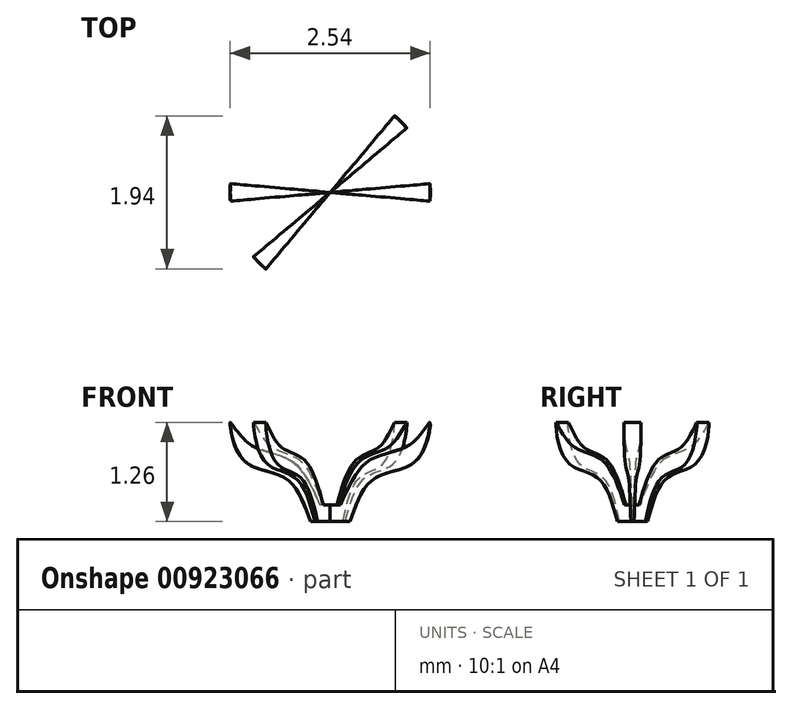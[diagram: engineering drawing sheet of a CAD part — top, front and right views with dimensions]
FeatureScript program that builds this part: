
annotation { "Feature Type Name" : "Feature", "Feature Type Description" : "" }
export const myFeature = defineFeature(function(context is Context, id is Id, definition is map)
    precondition{}
    {
        {
            var Q0;
            Q0=qCreatedBy(makeId("Front.planeOp"),FACE);
            var sketch = newSketch(context, id + "F0", { "sketchPlane" : qUnion([Q0])});
            skFitSpline(sketch, "E0", {"points": [v(-0.25, 0) * mm, v(-0.58, 0.55) * mm, v(-1.12, 0.8) * mm, v(-1.27, 1.25) * mm, v(-1.27, 1.26) * mm], "startDerivative": vector(-0.7, 1.99) * mm, "endDerivative": vector(0.1, 0.08) * mm});
            skFitSpline(sketch, "E1", {"points": [v(-1.27, 1.26) * mm, v(-0.95, 0.94) * mm, v(-0.5, 0.77) * mm, v(-0.13, 0.2) * mm], "startDerivative": vector(0.89, -1.24) * mm, "endDerivative": vector(0.8, -1.8) * mm});
            skLineSegment(sketch, "E2", {"start": v(-0.25, 0) * mm, "end": v(0, 0) * mm});
            skLineSegment(sketch, "E3", {"start": v(0, 0) * mm, "end": v(0, 0.2) * mm});
            skLineSegment(sketch, "E4", {"start": v(0, 0.2) * mm, "end": v(-0.13, 0.2) * mm});
            skSolve(sketch);
        }
        {
            var Q0;
            Q0=makeQuery(id+"F0.imprint","IMPRINT",FACE,{"disambiguationData":[TD([[makeQuery(id+"F0.imprint","IMPRINT",EDGE,{"derivedFrom":sQuery(id+"F0.wireOp",EDGE,"E0")}),-1.0]])]});
            var Q1;
            Q1=sQuery(id+"F0.wireOp",EDGE,"E3");
            revolve(context, id + "F1", {"surfaceOperationType" : NewSurfaceOperationType.NEW, "entities" : qUnion([Q0]), "axis" : qUnion([Q1]), "revolveType" : RevolveType.SYMMETRIC, "oppositeDirection" : true, "angle" : 10 * degree});
        }
        {
            var Q0;
            Q0=makeQuery(id+"F1.opRevolve","SWEPT_BODY",BODY,{"disambiguationData":[OSD([sQuery(id+"F0.wireOp",EDGE,"E0"),sQuery(id+"F0.wireOp",EDGE,"E1"),sQuery(id+"F0.wireOp",EDGE,"E2"),sQuery(id+"F0.wireOp",EDGE,"E3"),sQuery(id+"F0.wireOp",EDGE,"E4")])]});
            var Q1;
            Q1=makeQuery(id+"F1.opRevolve","CAP_EDGE",EDGE,{"disambiguationData":[OSD([sQuery(id+"F0.wireOp",EDGE,"E3")])],"isStart":true});
            circularPattern(context, id + "F2", {"entities" : qUnion([Q0]), "axis" : qUnion([Q1]), "angle" : 45 * degree, "instanceCount" : 2, "equalSpace" : true});
        }
        {
            var Q0;
            Q0=makeQuery(id+"F1.opRevolve","SWEPT_BODY",BODY,{"disambiguationData":[OSD([sQuery(id+"F0.wireOp",EDGE,"E0"),sQuery(id+"F0.wireOp",EDGE,"E1"),sQuery(id+"F0.wireOp",EDGE,"E2"),sQuery(id+"F0.wireOp",EDGE,"E3"),sQuery(id+"F0.wireOp",EDGE,"E4")])]});
            var Q1;
            Q1=makeQuery(id+"F2.opPattern","COPY",BODY,{"derivedFrom":makeQuery(id+"F1.opRevolve","SWEPT_BODY",BODY,{"disambiguationData":[OSD([sQuery(id+"F0.wireOp",EDGE,"E0"),sQuery(id+"F0.wireOp",EDGE,"E1"),sQuery(id+"F0.wireOp",EDGE,"E2"),sQuery(id+"F0.wireOp",EDGE,"E3"),sQuery(id+"F0.wireOp",EDGE,"E4")])]}),"instanceName":"1"});
            var Q2;
            Q2=makeQuery(id+"F1.opRevolve","CAP_EDGE",EDGE,{"disambiguationData":[OSD([sQuery(id+"F0.wireOp",EDGE,"E3")])],"isStart":true});
            circularPattern(context, id + "F3", {"entities" : qUnion([Q0, Q1]), "axis" : qUnion([Q2]), "angle" : 360 * degree, "instanceCount" : 2, "equalSpace" : true});
        }
    });
